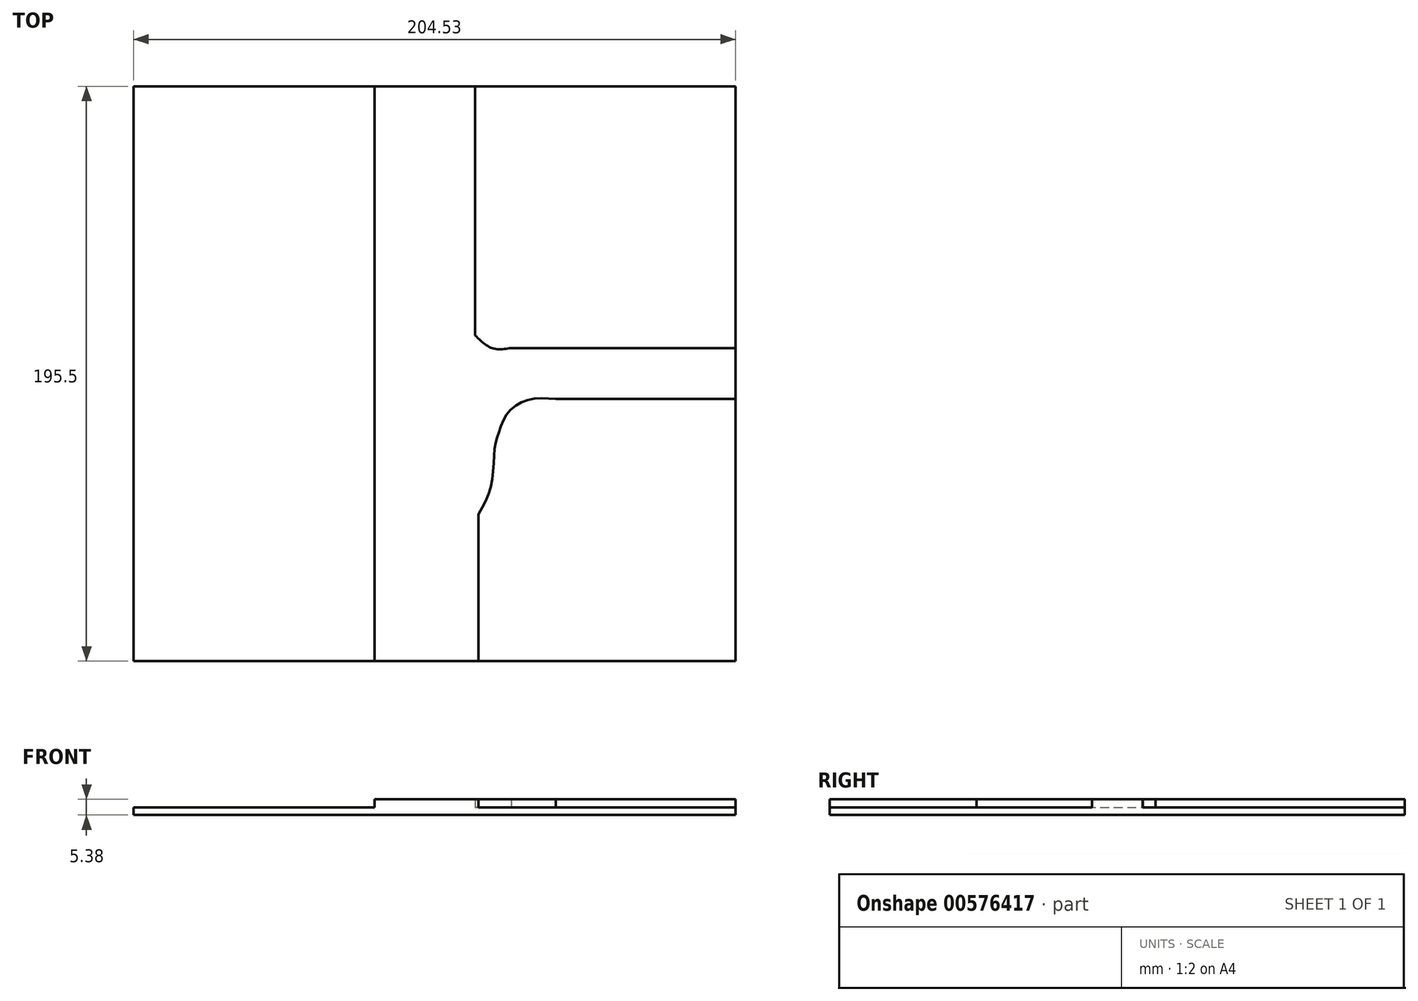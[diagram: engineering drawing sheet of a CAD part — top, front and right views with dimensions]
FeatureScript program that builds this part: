
annotation { "Feature Type Name" : "Feature", "Feature Type Description" : "" }
export const myFeature = defineFeature(function(context is Context, id is Id, definition is map)
    precondition{}
    {
        {
            var Q0;
            Q0=qCreatedBy(makeId("Top.planeOp"),FACE);
            var sketch = newSketch(context, id + "F0", { "sketchPlane" : qUnion([Q0])});
            skLineSegment(sketch, "E0.bottom", {"start": v(-99.29, 101.7) * mm, "end": v(105.24, 101.7) * mm});
            skLineSegment(sketch, "E0.top", {"start": v(-99.29, -93.8) * mm, "end": v(105.24, -93.8) * mm});
            skLineSegment(sketch, "E0.left", {"start": v(-99.29, 101.7) * mm, "end": v(-99.29, -93.8) * mm});
            skLineSegment(sketch, "E0.right", {"start": v(105.24, 101.7) * mm, "end": v(105.24, -93.8) * mm});
            skSolve(sketch);
        }
        {
            var Q0;
            Q0=makeQuery(id+"F0.imprint","IMPRINT",FACE,{"disambiguationData":[TD([[makeQuery(id+"F0.imprint","IMPRINT",EDGE,{"derivedFrom":sQuery(id+"F0.wireOp",EDGE,"E0.bottom")}),-1.0]])]});
            extrude(context, id + "F1", {"entities" : qUnion([Q0]), "depth" : 2.54 * mm, "offsetDistance" : 25.4 * mm});
        }
        {
            var Q0;
            Q0=makeQuery(id+"F1.opExtrude","CAP_FACE",FACE,{"disambiguationData":[OSD([sQuery(id+"F0.wireOp",EDGE,"E0.bottom"),sQuery(id+"F0.wireOp",EDGE,"E0.top"),sQuery(id+"F0.wireOp",EDGE,"E0.left"),sQuery(id+"F0.wireOp",EDGE,"E0.right")])],"isStart":false});
            var sketch = newSketch(context, id + "F2", { "sketchPlane" : qUnion([Q0])});
            skLineSegment(sketch, "E1", {"start": v(-17.38, -93.8) * mm, "end": v(-17.38, -43.13) * mm});
            skLineSegment(sketch, "E2", {"start": v(17.9, -93.8) * mm, "end": v(17.9, -43.85) * mm});
            skFitSpline(sketch, "E3", {"points": [v(17.9, -43.85) * mm, v(22.21, -34.14) * mm, v(23.3, -22.62) * mm, v(24.73, -16.14) * mm, v(27.97, -9.3) * mm, v(34.81, -4.98) * mm, v(44.17, -4.62) * mm], "startDerivative": vector(28.7, 50.1) * mm, "endDerivative": vector(56.5, -3.47) * mm});
            skLineSegment(sketch, "E4", {"start": v(44.17, -4.62) * mm, "end": v(105.24, -4.62) * mm});
            skLineSegment(sketch, "E5", {"start": v(105.24, 12.66) * mm, "end": v(36.25, 12.66) * mm});
            skLineSegment(sketch, "E6", {"start": v(36.25, 12.66) * mm, "end": v(29.05, 12.66) * mm});
            skPoint(sketch, "E7.1.internal.snap0", {"position": v(32.65, 12.66) * mm});
            skFitSpline(sketch, "E7", {"points": [v(29.05, 12.66) * mm, v(22.44, 12.66) * mm, v(16.74, 17) * mm], "startDerivative": vector(-14.06, -2.08) * mm, "endDerivative": vector(-10.58, 10.67) * mm});
            skLineSegment(sketch, "E8", {"start": v(16.74, 17) * mm, "end": v(16.74, 101.7) * mm});
            skLineSegment(sketch, "E9", {"start": v(105.24, 12.66) * mm, "end": v(105.24, -4.62) * mm});
            skLineSegment(sketch, "E10", {"start": v(-17.38, -43.13) * mm, "end": v(-17.38, 101.7) * mm});
            skLineSegment(sketch, "E11", {"start": v(-17.38, 101.7) * mm, "end": v(16.74, 101.7) * mm});
            skLineSegment(sketch, "E12", {"start": v(-17.38, -93.8) * mm, "end": v(17.9, -93.8) * mm});
            skSolve(sketch);
        }
        {
            var Q0;
            Q0=makeQuery(id+"F2.imprint","IMPRINT",FACE,{"disambiguationData":[TD([[makeQuery(id+"F2.imprint","IMPRINT",EDGE,{"derivedFrom":sQuery(id+"F2.wireOp",EDGE,"E1")}),-1.0]])]});
            extrude(context, id + "F3", {"entities" : qUnion([Q0]), "operationType" : NewBodyOperationType.ADD, "depth" : 2.84 * mm, "offsetDistance" : 25.4 * mm});
        }
    });
